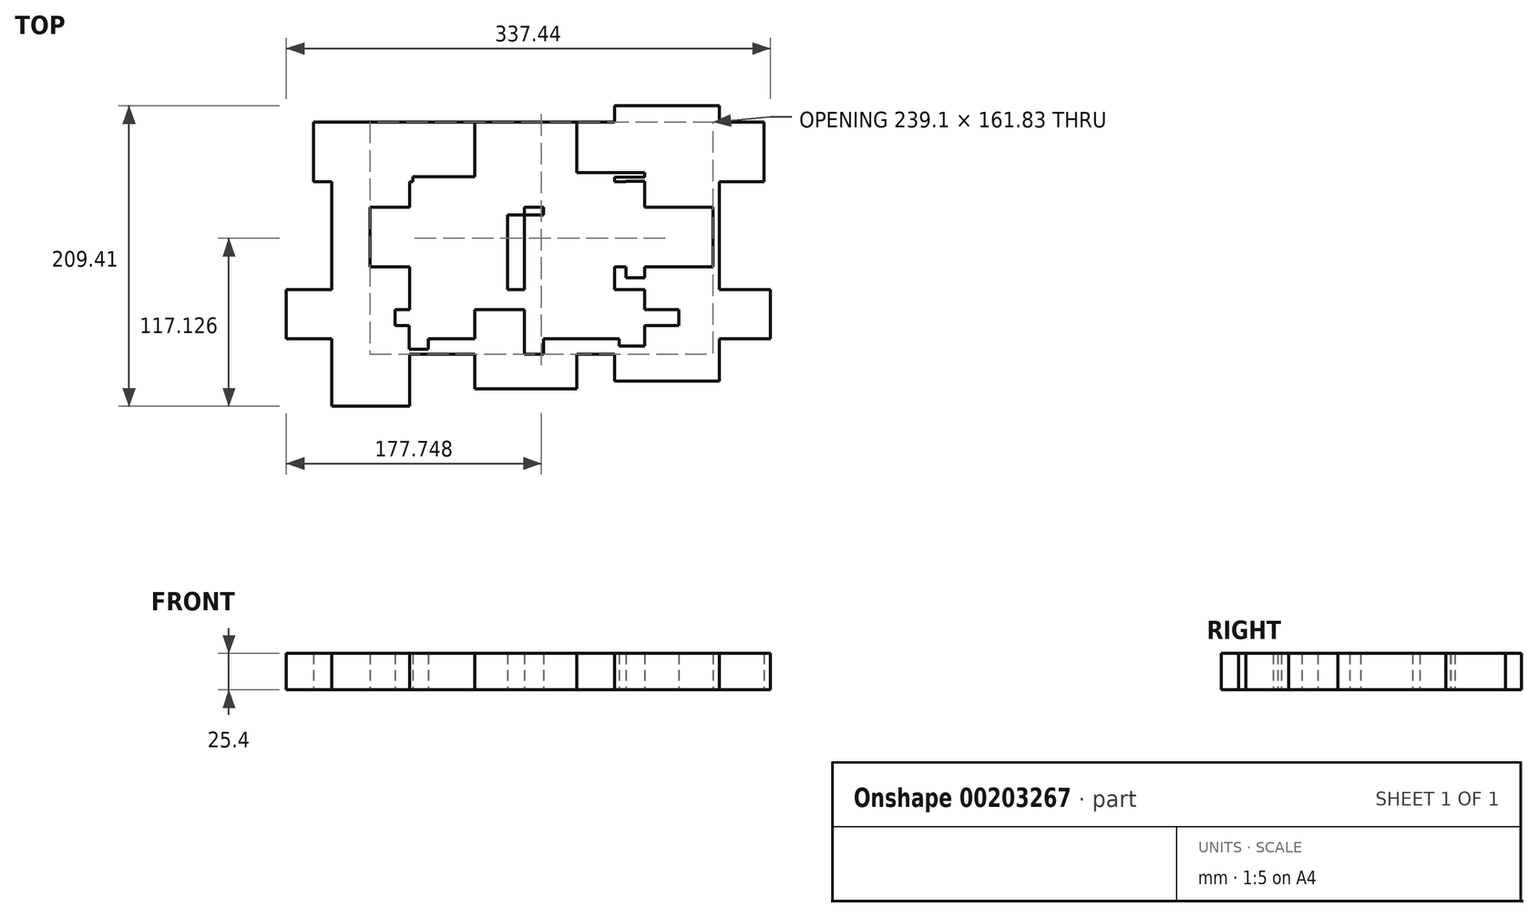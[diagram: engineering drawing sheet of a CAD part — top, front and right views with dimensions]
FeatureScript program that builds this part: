
annotation { "Feature Type Name" : "Feature", "Feature Type Description" : "" }
export const myFeature = defineFeature(function(context is Context, id is Id, definition is map)
    precondition{}
    {
        {
            var Q0;
            Q0=qCreatedBy(makeId("Top.planeOp"),FACE);
            var sketch = newSketch(context, id + "F0", { "sketchPlane" : qUnion([Q0])});
            skLineSegment(sketch, "E0.bottom", {"start": v(0, 0) * mm, "end": v(-39.62, 0) * mm});
            skLineSegment(sketch, "E0.top", {"start": v(0, -52.11) * mm, "end": v(-39.62, -52.11) * mm});
            skLineSegment(sketch, "E0.left", {"start": v(0, 0) * mm, "end": v(0, -52.11) * mm});
            skLineSegment(sketch, "E0.right", {"start": v(-39.62, 0) * mm, "end": v(-39.62, -52.11) * mm});
            skLineSegment(sketch, "E1.bottom", {"start": v(35.8, -33.12) * mm, "end": v(-86.46, -33.12) * mm});
            skLineSegment(sketch, "E1.top", {"start": v(35.8, -21.23) * mm, "end": v(-86.46, -21.23) * mm});
            skLineSegment(sketch, "E1.left", {"start": v(35.8, -33.12) * mm, "end": v(35.8, -21.23) * mm});
            skLineSegment(sketch, "E1.right", {"start": v(-86.46, -33.12) * mm, "end": v(-86.46, -21.23) * mm});
            skLineSegment(sketch, "E2.bottom", {"start": v(-14.56, 22.65) * mm, "end": v(-28.08, 22.65) * mm});
            skLineSegment(sketch, "E2.top", {"start": v(-14.56, -97.27) * mm, "end": v(-28.08, -97.27) * mm});
            skLineSegment(sketch, "E2.left", {"start": v(-14.56, 22.65) * mm, "end": v(-14.56, -97.27) * mm});
            skLineSegment(sketch, "E2.right", {"start": v(-28.08, 22.65) * mm, "end": v(-28.08, -97.27) * mm});
            skLineSegment(sketch, "E3.bottom", {"start": v(-10.17, 26.17) * mm, "end": v(55.88, 26.17) * mm});
            skLineSegment(sketch, "E3.top", {"start": v(-10.17, 29.43) * mm, "end": v(55.88, 29.43) * mm});
            skLineSegment(sketch, "E3.left", {"start": v(-10.17, 26.17) * mm, "end": v(-10.17, 29.43) * mm});
            skLineSegment(sketch, "E3.right", {"start": v(55.88, 26.17) * mm, "end": v(55.88, 29.43) * mm});
            skLineSegment(sketch, "E4.bottom", {"start": v(55.88, 23.29) * mm, "end": v(42.71, 23.29) * mm});
            skLineSegment(sketch, "E4.top", {"start": v(55.88, -43.78) * mm, "end": v(42.71, -43.78) * mm});
            skLineSegment(sketch, "E4.left", {"start": v(55.88, 23.29) * mm, "end": v(55.88, -43.78) * mm});
            skLineSegment(sketch, "E4.right", {"start": v(42.71, 23.29) * mm, "end": v(42.71, -43.78) * mm});
            skLineSegment(sketch, "E5.bottom", {"start": v(-32.53, 26.55) * mm, "end": v(-105.58, 26.55) * mm});
            skLineSegment(sketch, "E5.top", {"start": v(-32.53, 23.05) * mm, "end": v(-105.58, 23.05) * mm});
            skLineSegment(sketch, "E5.left", {"start": v(-32.53, 26.55) * mm, "end": v(-32.53, 23.05) * mm});
            skLineSegment(sketch, "E5.right", {"start": v(-105.58, 26.55) * mm, "end": v(-105.58, 23.05) * mm});
            skLineSegment(sketch, "E6.bottom", {"start": v(-94.45, 23.05) * mm, "end": v(-107.86, 23.05) * mm});
            skLineSegment(sketch, "E6.top", {"start": v(-94.45, -65.18) * mm, "end": v(-107.86, -65.18) * mm});
            skLineSegment(sketch, "E6.left", {"start": v(-94.45, 23.05) * mm, "end": v(-94.45, -65.18) * mm});
            skLineSegment(sketch, "E6.right", {"start": v(-107.86, 23.05) * mm, "end": v(-107.86, -65.18) * mm});
            skLineSegment(sketch, "E7.bottom", {"start": v(-35.53, -97.27) * mm, "end": v(-115.58, -97.27) * mm});
            skLineSegment(sketch, "E7.top", {"start": v(-35.53, -97.27) * mm, "end": v(-115.58, -97.27) * mm});
            skLineSegment(sketch, "E7.left", {"start": v(-35.53, -97.27) * mm, "end": v(-35.53, -97.27) * mm});
            skLineSegment(sketch, "E7.right", {"start": v(-115.58, -97.27) * mm, "end": v(-115.58, -97.27) * mm});
            skLineSegment(sketch, "E8.bottom", {"start": v(-8.38, -97.27) * mm, "end": v(52.48, -97.27) * mm});
            skLineSegment(sketch, "E8.top", {"start": v(-8.38, -97.27) * mm, "end": v(52.48, -97.27) * mm});
            skLineSegment(sketch, "E8.left", {"start": v(-8.38, -97.27) * mm, "end": v(-8.38, -97.27) * mm});
            skLineSegment(sketch, "E8.right", {"start": v(52.48, -97.27) * mm, "end": v(52.48, -97.27) * mm});
            skLineSegment(sketch, "E9.bottom", {"start": v(38.13, -91.48) * mm, "end": v(55.88, -91.48) * mm});
            skLineSegment(sketch, "E9.top", {"start": v(38.13, -52.11) * mm, "end": v(55.88, -52.11) * mm});
            skLineSegment(sketch, "E9.left", {"start": v(38.13, -91.48) * mm, "end": v(38.13, -52.11) * mm});
            skLineSegment(sketch, "E9.right", {"start": v(55.88, -91.48) * mm, "end": v(55.88, -52.11) * mm});
            skLineSegment(sketch, "E10.bottom", {"start": v(-108.15, -71.97) * mm, "end": v(-94.92, -71.97) * mm});
            skLineSegment(sketch, "E10.top", {"start": v(-108.15, -93.91) * mm, "end": v(-94.92, -93.91) * mm});
            skLineSegment(sketch, "E10.left", {"start": v(-108.15, -71.97) * mm, "end": v(-108.15, -93.91) * mm});
            skLineSegment(sketch, "E10.right", {"start": v(-94.92, -71.97) * mm, "end": v(-94.92, -93.91) * mm});
            skLineSegment(sketch, "E11.bottom", {"start": v(-135.68, -36.3) * mm, "end": v(103.42, -36.3) * mm});
            skLineSegment(sketch, "E11.top", {"start": v(-135.68, 5.18) * mm, "end": v(103.42, 5.18) * mm});
            skLineSegment(sketch, "E11.left", {"start": v(-135.68, -36.3) * mm, "end": v(-135.68, 5.18) * mm});
            skLineSegment(sketch, "E11.right", {"start": v(103.42, -36.3) * mm, "end": v(103.42, 5.18) * mm});
            skLineSegment(sketch, "E12.bottom", {"start": v(-118, -66.24) * mm, "end": v(79.77, -66.24) * mm});
            skLineSegment(sketch, "E12.top", {"start": v(-118, -77.3) * mm, "end": v(79.77, -77.3) * mm});
            skLineSegment(sketch, "E12.left", {"start": v(-118, -66.24) * mm, "end": v(-118, -77.3) * mm});
            skLineSegment(sketch, "E12.right", {"start": v(79.77, -66.24) * mm, "end": v(79.77, -77.3) * mm});
            skLineSegment(sketch, "E13.bottom", {"start": v(8.43, 64.56) * mm, "end": v(-62.61, 64.56) * mm});
            skLineSegment(sketch, "E13.top", {"start": v(8.43, -121.32) * mm, "end": v(-62.61, -121.32) * mm});
            skLineSegment(sketch, "E13.left", {"start": v(8.43, 64.56) * mm, "end": v(8.43, -121.32) * mm});
            skLineSegment(sketch, "E13.right", {"start": v(-62.61, 64.56) * mm, "end": v(-62.61, -121.32) * mm});
            skLineSegment(sketch, "E14.bottom", {"start": v(107.88, 75.93) * mm, "end": v(34.92, 75.93) * mm});
            skLineSegment(sketch, "E14.top", {"start": v(107.88, -116.14) * mm, "end": v(34.92, -116.14) * mm});
            skLineSegment(sketch, "E14.left", {"start": v(107.88, 75.93) * mm, "end": v(107.88, -116.14) * mm});
            skLineSegment(sketch, "E14.right", {"start": v(34.92, 75.93) * mm, "end": v(34.92, -116.14) * mm});
            skLineSegment(sketch, "E15.bottom", {"start": v(-107.86, 57.3) * mm, "end": v(-162.25, 57.3) * mm});
            skLineSegment(sketch, "E15.top", {"start": v(-107.86, -133.48) * mm, "end": v(-162.25, -133.48) * mm});
            skLineSegment(sketch, "E15.left", {"start": v(-107.86, 57.3) * mm, "end": v(-107.86, -133.48) * mm});
            skLineSegment(sketch, "E15.right", {"start": v(-162.25, 57.3) * mm, "end": v(-162.25, -133.48) * mm});
            skLineSegment(sketch, "E16.bottom", {"start": v(-193.88, -86.5) * mm, "end": v(143.56, -86.5) * mm});
            skLineSegment(sketch, "E16.top", {"start": v(-193.88, -52.11) * mm, "end": v(143.56, -52.11) * mm});
            skLineSegment(sketch, "E16.left", {"start": v(-193.88, -86.5) * mm, "end": v(-193.88, -52.11) * mm});
            skLineSegment(sketch, "E16.right", {"start": v(143.56, -86.5) * mm, "end": v(143.56, -52.11) * mm});
            skLineSegment(sketch, "E17.bottom", {"start": v(-174.9, 23.05) * mm, "end": v(139.03, 23.05) * mm});
            skLineSegment(sketch, "E17.top", {"start": v(-174.9, 64.75) * mm, "end": v(139.03, 64.75) * mm});
            skLineSegment(sketch, "E17.left", {"start": v(-174.9, 23.05) * mm, "end": v(-174.9, 64.75) * mm});
            skLineSegment(sketch, "E17.right", {"start": v(139.03, 23.05) * mm, "end": v(139.03, 64.75) * mm});
            skSolve(sketch);
        }
        {
            var Q0;
            Q0 = qSketchRegion(id + "F0", true);
            var Q1;
            {var subQ0=sQuery(id+"F0.wireOp",EDGE,"E2.left");var subQ1=sQuery(id+"F0.wireOp",EDGE,"E0.bottom");var subQ2=makeQuery(id+"F0.imprint","INTERSECT",VERTEX,{"derivedFrom":[subQ1,subQ0]});Q1=makeQuery(id+"F0.imprint","IMPRINT",FACE,{"disambiguationData":[TD([[makeQuery(id+"F0.imprint","IMPRINT",EDGE,{"disambiguationData":[TD([[subQ2,-1.0]])],"derivedFrom":subQ1}),-1.0]])]});}
            var Q2;
            {var subQ0=sQuery(id+"F0.wireOp",EDGE,"E16.top");var subQ6=sQuery(id+"F0.wireOp",EDGE,"E2.right");var subQ7=makeQuery(id+"F0.imprint","INTERSECT",VERTEX,{"derivedFrom":[subQ6,subQ0]});Q2=makeQuery(id+"F0.imprint","IMPRINT",FACE,{"disambiguationData":[TD([[makeQuery(id+"F0.imprint","IMPRINT",EDGE,{"disambiguationData":[TD([[subQ7,-1.0]])],"derivedFrom":subQ6}),-1.0]])]});}
            extrude(context, id + "F1", {"entities" : qUnion([Q0, Q1, Q2]), "depth" : 25.4 * mm});
        }
    });
